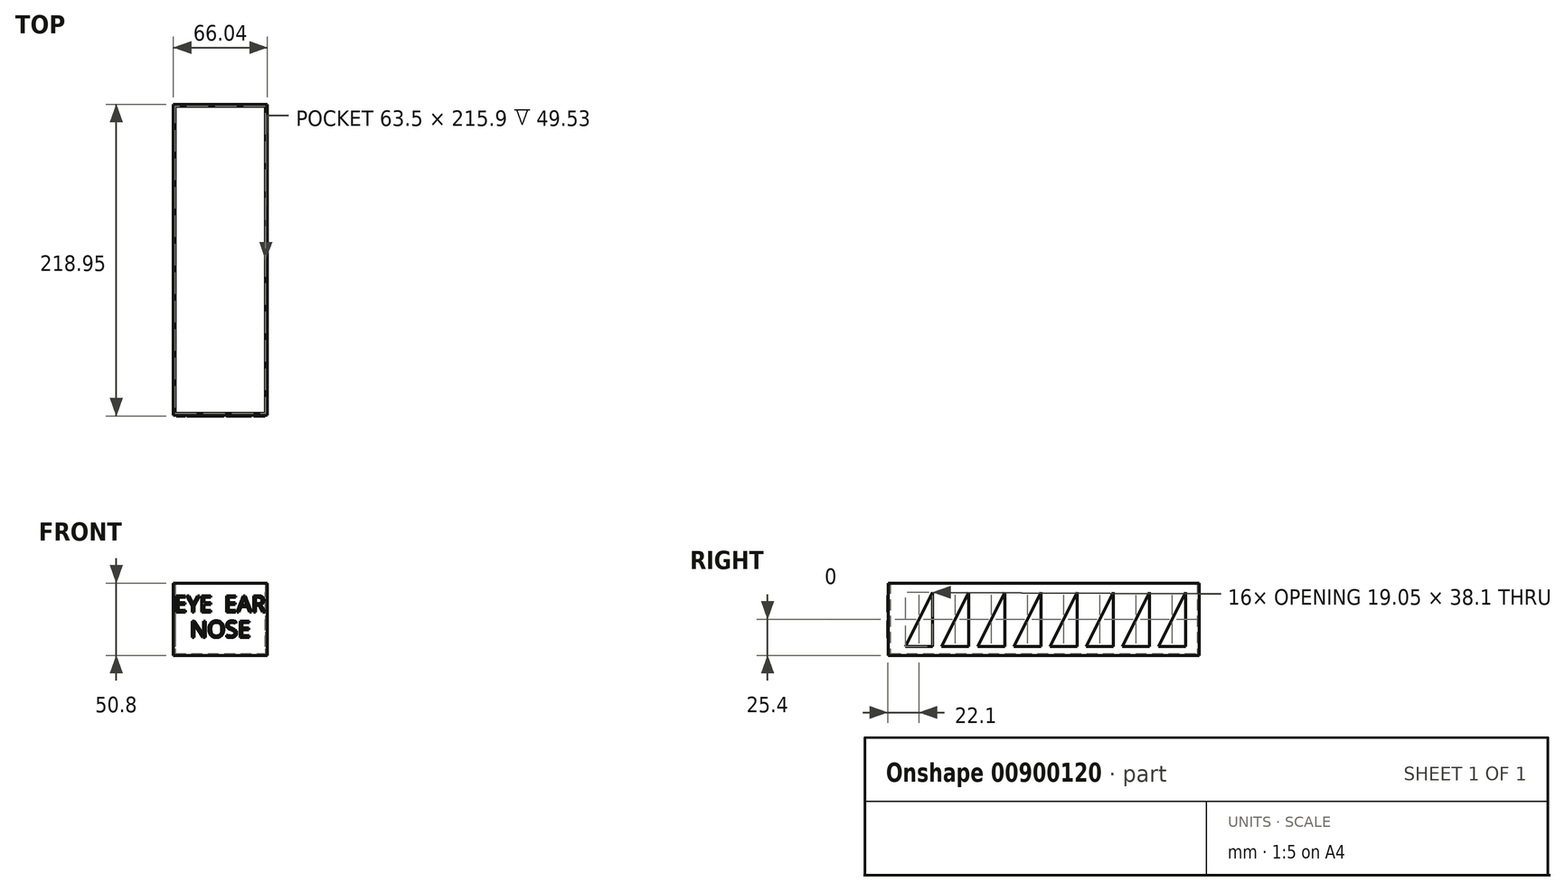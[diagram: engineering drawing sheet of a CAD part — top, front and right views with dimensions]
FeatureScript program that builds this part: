
annotation { "Feature Type Name" : "Feature", "Feature Type Description" : "" }
export const myFeature = defineFeature(function(context is Context, id is Id, definition is map)
    precondition{}
    {
        {
            var Q0;
            Q0=qCreatedBy(makeId("Top.planeOp"),FACE);
            var sketch = newSketch(context, id + "F0", { "sketchPlane" : qUnion([Q0])});
            skLineSegment(sketch, "E0.bottom", {"start": v(31.75, 107.95) * mm, "end": v(-31.75, 107.95) * mm});
            skLineSegment(sketch, "E0.top", {"start": v(31.75, -107.95) * mm, "end": v(-31.75, -107.95) * mm});
            skLineSegment(sketch, "E0.left", {"start": v(31.75, 107.95) * mm, "end": v(31.75, -107.95) * mm});
            skLineSegment(sketch, "E0.right", {"start": v(-31.75, 107.95) * mm, "end": v(-31.75, -107.95) * mm});
            skPoint(sketch, "E0.middle", {"position": v(0, 0) * mm});
            skLineSegment(sketch, "E1.0", {"start": v(33.02, 109.22) * mm, "end": v(-33.02, 109.22) * mm});
            skLineSegment(sketch, "E1.1", {"start": v(33.02, 109.22) * mm, "end": v(33.02, -109.22) * mm});
            skLineSegment(sketch, "E1.2", {"start": v(33.02, -109.22) * mm, "end": v(-33.02, -109.22) * mm});
            skLineSegment(sketch, "E1.3", {"start": v(-33.02, 109.22) * mm, "end": v(-33.02, -109.22) * mm});
            skSolve(sketch);
        }
        {
            var Q0;
            Q0=qSketchRegion(id+"F0",true);
            var Q1;
            Q1=makeQuery(id+"F0.imprint","IMPRINT",FACE,{"disambiguationData":[TD([[makeQuery(id+"F0.imprint","IMPRINT",EDGE,{"derivedFrom":sQuery(id+"F0.wireOp",EDGE,"E0.bottom")}),1.0]])]});
            extrude(context, id + "F1", {"entities" : qUnion([Q0, Q1]), "depth" : 1.27 * mm, "offsetDistance" : 25.4 * mm});
        }
        {
            var Q0;
            Q0=qSketchRegion(id+"F0",true);
            extrude(context, id + "F2", {"entities" : qUnion([Q0]), "operationType" : NewBodyOperationType.ADD, "depth" : 50.8 * mm, "offsetDistance" : 25.4 * mm});
        }
        {
            var Q0;
            {var subQ0=sQuery(id+"F0.wireOp",EDGE,"E1.3");Q0=makeQuery(id+"F2.boolean.opBoolean","MERGE",FACE,{"derivedFrom":[makeQuery(id+"F1.opExtrude","SWEPT_FACE",FACE,{"disambiguationData":[OSD([subQ0])]}),makeQuery(id+"F2.opExtrude","SWEPT_FACE",FACE,{"disambiguationData":[OSD([subQ0])]})]});}
            var sketch = newSketch(context, id + "F3", { "sketchPlane" : qUnion([Q0])});
            skLineSegment(sketch, "E2", {"start": v(-99.7, 44.45) * mm, "end": v(-99.7, 6.35) * mm});
            skLineSegment(sketch, "E3", {"start": v(-99.7, 6.35) * mm, "end": v(-80.65, 6.35) * mm});
            skLineSegment(sketch, "E4", {"start": v(-80.64, 6.35) * mm, "end": v(-99.7, 44.45) * mm});
            skLineSegment(sketch, "E5.1.0.0", {"start": v(-55.25, 6.35) * mm, "end": v(-74.3, 44.45) * mm});
            skLineSegment(sketch, "E5.1.0.1", {"start": v(-74.3, 44.45) * mm, "end": v(-74.3, 6.35) * mm});
            skLineSegment(sketch, "E5.1.0.2", {"start": v(-74.3, 44.45) * mm, "end": v(-74.3, 44.45) * mm});
            skLineSegment(sketch, "E5.1.0.3", {"start": v(-74.3, 6.35) * mm, "end": v(-55.25, 6.35) * mm});
            skLineSegment(sketch, "E5.2.0.0", {"start": v(-29.85, 6.35) * mm, "end": v(-48.9, 44.45) * mm});
            skLineSegment(sketch, "E5.2.0.1", {"start": v(-48.9, 44.45) * mm, "end": v(-48.9, 6.35) * mm});
            skLineSegment(sketch, "E5.2.0.2", {"start": v(-48.9, 44.45) * mm, "end": v(-48.9, 44.45) * mm});
            skLineSegment(sketch, "E5.2.0.3", {"start": v(-48.9, 6.35) * mm, "end": v(-29.85, 6.35) * mm});
            skLineSegment(sketch, "E5.3.0.0", {"start": v(-4.45, 6.35) * mm, "end": v(-23.5, 44.45) * mm});
            skLineSegment(sketch, "E5.3.0.1", {"start": v(-23.5, 44.45) * mm, "end": v(-23.5, 6.35) * mm});
            skLineSegment(sketch, "E5.3.0.2", {"start": v(-23.5, 44.45) * mm, "end": v(-23.5, 44.45) * mm});
            skLineSegment(sketch, "E5.3.0.3", {"start": v(-23.5, 6.35) * mm, "end": v(-4.45, 6.35) * mm});
            skLineSegment(sketch, "E5.4.0.0", {"start": v(20.95, 6.35) * mm, "end": v(1.9, 44.45) * mm});
            skLineSegment(sketch, "E5.4.0.1", {"start": v(1.9, 44.45) * mm, "end": v(1.9, 6.35) * mm});
            skLineSegment(sketch, "E5.4.0.2", {"start": v(1.9, 44.45) * mm, "end": v(1.9, 44.45) * mm});
            skLineSegment(sketch, "E5.4.0.3", {"start": v(1.9, 6.35) * mm, "end": v(20.95, 6.35) * mm});
            skLineSegment(sketch, "E5.5.0.0", {"start": v(46.35, 6.35) * mm, "end": v(27.3, 44.45) * mm});
            skLineSegment(sketch, "E5.5.0.1", {"start": v(27.3, 44.45) * mm, "end": v(27.3, 6.35) * mm});
            skLineSegment(sketch, "E5.5.0.2", {"start": v(27.3, 44.45) * mm, "end": v(27.3, 44.45) * mm});
            skLineSegment(sketch, "E5.5.0.3", {"start": v(27.3, 6.35) * mm, "end": v(46.35, 6.35) * mm});
            skLineSegment(sketch, "E5.6.0.0", {"start": v(71.75, 6.35) * mm, "end": v(52.7, 44.45) * mm});
            skLineSegment(sketch, "E5.6.0.1", {"start": v(52.7, 44.45) * mm, "end": v(52.7, 6.35) * mm});
            skLineSegment(sketch, "E5.6.0.2", {"start": v(52.7, 44.45) * mm, "end": v(52.7, 44.45) * mm});
            skLineSegment(sketch, "E5.6.0.3", {"start": v(52.7, 6.35) * mm, "end": v(71.75, 6.35) * mm});
            skLineSegment(sketch, "E5.7.0.0", {"start": v(97.15, 6.35) * mm, "end": v(78.1, 44.45) * mm});
            skLineSegment(sketch, "E5.7.0.1", {"start": v(78.1, 44.45) * mm, "end": v(78.1, 6.35) * mm});
            skLineSegment(sketch, "E5.7.0.2", {"start": v(78.1, 44.45) * mm, "end": v(78.1, 44.45) * mm});
            skLineSegment(sketch, "E5.7.0.3", {"start": v(78.1, 6.35) * mm, "end": v(97.15, 6.35) * mm});
            skLineSegment(sketch, "E5.direction1", {"start": v(-80.65, 6.35) * mm, "end": v(-55.25, 6.35) * mm, "construction": true});
            skSolve(sketch);
        }
        {
            var Q0;
            Q0=qSketchRegion(id+"F3",true);
            extrude(context, id + "F4", {"entities" : qUnion([Q0]), "operationType" : NewBodyOperationType.REMOVE, "oppositeDirection" : true, "depth" : 76.2 * mm, "offsetDistance" : 25.4 * mm});
        }
        {
            var Q0;
            {var subQ0=sQuery(id+"F0.wireOp",EDGE,"E1.2");Q0=makeQuery(id+"F2.boolean.opBoolean","MERGE",FACE,{"derivedFrom":[makeQuery(id+"F1.opExtrude","SWEPT_FACE",FACE,{"disambiguationData":[OSD([subQ0])]}),makeQuery(id+"F2.opExtrude","SWEPT_FACE",FACE,{"disambiguationData":[OSD([subQ0])]})]});}
            var sketch = newSketch(context, id + "F5", { "sketchPlane" : qUnion([Q0])});
            skText(sketch, "E6", { "text": "EYE  EAR", "fontName": "OpenSans-Regular.ttf"});
            skText(sketch, "E7", { "text": "NOSE", "fontName": "OpenSans-Regular.ttf"});
            const initialGuessF5  = {"E6": [-0.03248, 0.03048, 1, 0, 0.01156], "E7": [-0.0212, 0.0127, 1, 0, 0.01156]};
            skSetInitialGuess(sketch, initialGuessF5);
            skSolve(sketch);
        }
        {
            var Q0;
            Q0=qSketchRegion(id+"F5",true);
            extrude(context, id + "F6", {"entities" : qUnion([Q0]), "operationType" : NewBodyOperationType.ADD, "depth" : 0.5 * mm, "offsetDistance" : 25.4 * mm});
        }
    });
